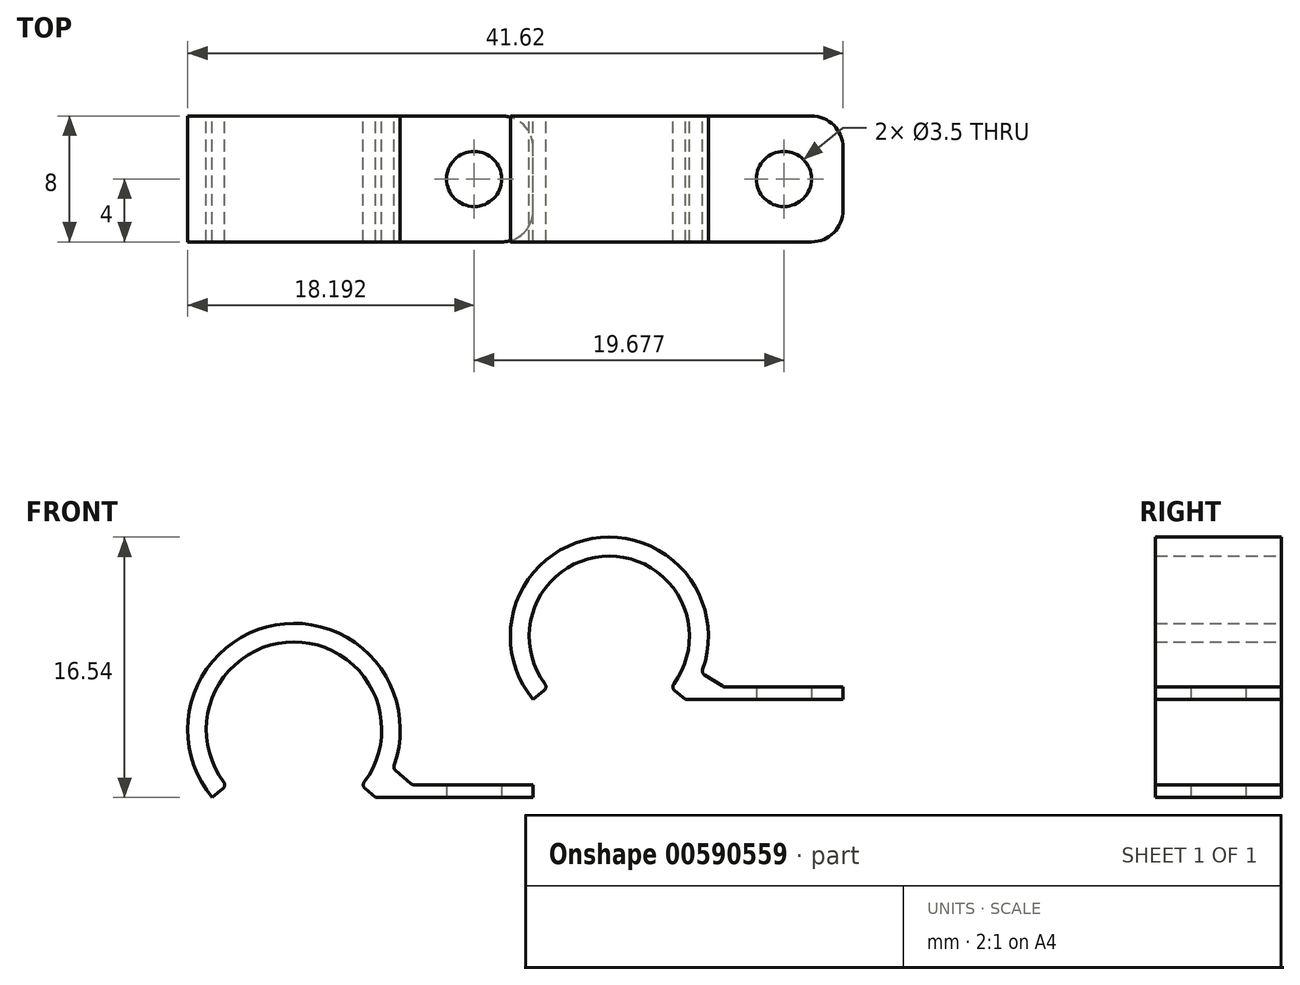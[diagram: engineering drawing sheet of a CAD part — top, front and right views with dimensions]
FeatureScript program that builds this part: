
annotation { "Feature Type Name" : "Feature", "Feature Type Description" : "" }
export const myFeature = defineFeature(function(context is Context, id is Id, definition is map)
    precondition{}
    {
        {
            var Q0;
            Q0=qCreatedBy(makeId("Front.planeOp"),FACE);
            var sketch = newSketch(context, id + "F0", { "sketchPlane" : qUnion([Q0])});
            skArc(sketch, "E0", {"start": v(-11.13, 19.13) * mm, "mid": v(-11.18, 8) * mm, "end": v(-11.03, 19.13) * mm});
            skArc(sketch, "E1", {"start": v(-12.13, 20.56) * mm, "mid": v(-11.18, 6.5) * mm, "end": v(-10.03, 20.55) * mm});
            skLineSegment(sketch, "E2", {"start": v(-12.13, 19.04) * mm, "end": v(-12.13, 31.04) * mm});
            skLineSegment(sketch, "E3", {"start": v(-12.13, 31.04) * mm, "end": v(-11.13, 31.04) * mm});
            skLineSegment(sketch, "E4", {"start": v(-11.13, 31.04) * mm, "end": v(-11.13, 19.13) * mm});
            skLineSegment(sketch, "E5", {"start": v(-10.03, 19.02) * mm, "end": v(-10.03, 31.04) * mm});
            skLineSegment(sketch, "E6", {"start": v(-10.03, 31.04) * mm, "end": v(-11.03, 31.04) * mm});
            skLineSegment(sketch, "E7", {"start": v(-11.03, 31.04) * mm, "end": v(-11.03, 19.13) * mm});
            skArc(sketch, "E8", {"start": v(8.04, 19.7) * mm, "mid": v(8.99, 6.6) * mm, "end": v(10.14, 19.7) * mm});
            skLineSegment(sketch, "E9", {"start": v(8.04, 18.19) * mm, "end": v(8.04, 30.68) * mm});
            skLineSegment(sketch, "E10", {"start": v(8.04, 30.68) * mm, "end": v(9.04, 30.68) * mm});
            skLineSegment(sketch, "E11", {"start": v(9.04, 30.68) * mm, "end": v(9.04, 18.29) * mm});
            skLineSegment(sketch, "E12", {"start": v(10.14, 18.17) * mm, "end": v(10.14, 30.68) * mm});
            skLineSegment(sketch, "E13", {"start": v(10.14, 30.68) * mm, "end": v(9.14, 30.68) * mm});
            skLineSegment(sketch, "E14", {"start": v(9.14, 30.68) * mm, "end": v(9.14, 18.28) * mm});
            skArc(sketch, "E15", {"start": v(9.04, 18.29) * mm, "mid": v(8.99, 8.1) * mm, "end": v(9.14, 18.28) * mm});
            skCircle(sketch, "E16", {"center": v(-11.13, 7.24) * mm, "radius": 0.5 * mm});
            skCircle(sketch, "E17", {"center": v(9.04, 7.36) * mm, "radius": 0.5 * mm});
            skCircle(sketch, "E18", {"center": v(-11.13, 7.24) * mm, "radius": 0.45 * mm});
            skCircle(sketch, "E19", {"center": v(9.04, 7.36) * mm, "radius": 0.45 * mm});
            skLineSegment(sketch, "E20", {"start": v(-11.13, 8) * mm, "end": v(-11.13, 6.5) * mm});
            skLineSegment(sketch, "E21", {"start": v(9.04, 8.1) * mm, "end": v(9.04, 7.86) * mm});
            skLineSegment(sketch, "E22.trimOffspring", {"start": v(9.04, 6.86) * mm, "end": v(9.04, 6.6) * mm});
            skArc(sketch, "E23", {"start": v(8.78, 8.11) * mm, "mid": v(8.2, 7.38) * mm, "end": v(8.75, 6.61) * mm});
            skArc(sketch, "E24", {"start": v(9.36, 6.61) * mm, "mid": v(9.87, 7.36) * mm, "end": v(9.37, 8.12) * mm});
            skArc(sketch, "E25", {"start": v(8.7, 8.12) * mm, "mid": v(8.14, 7.39) * mm, "end": v(8.64, 6.62) * mm});
            skArc(sketch, "E26", {"start": v(9.47, 6.62) * mm, "mid": v(9.93, 7.38) * mm, "end": v(9.46, 8.12) * mm});
            skArc(sketch, "E27.converted", {"start": v(36.32, 10.08) * mm, "mid": v(31.86, 18.98) * mm, "end": v(27.4, 10.08) * mm});
            skArc(sketch, "E28.converted", {"start": v(38.22, 11.15) * mm, "mid": v(30.68, 20.06) * mm, "end": v(26.67, 9.1) * mm});
            skLineSegment(sketch, "E29", {"start": v(37.05, 9.1) * mm, "end": v(47.05, 9.1) * mm});
            skLineSegment(sketch, "E30", {"start": v(47.05, 9.1) * mm, "end": v(47.05, 9.9) * mm});
            skLineSegment(sketch, "E31", {"start": v(47.05, 9.9) * mm, "end": v(39.5, 9.9) * mm});
            skLineSegment(sketch, "E32", {"start": v(27.35, 9.67) * mm, "end": v(26.67, 9.1) * mm});
            skLineSegment(sketch, "E33", {"start": v(36.37, 9.67) * mm, "end": v(37.05, 9.1) * mm});
            skPoint(sketch, "E34.visualSharp", {"position": v(27.58, 9.85) * mm});
            skArc(sketch, "E34.filletArc", {"start": v(27.35, 9.67) * mm, "mid": v(27.46, 9.86) * mm, "end": v(27.4, 10.08) * mm});
            skPoint(sketch, "E35.visualSharp", {"position": v(36.14, 9.85) * mm});
            skArc(sketch, "E35.filletArc", {"start": v(36.32, 10.08) * mm, "mid": v(36.26, 9.86) * mm, "end": v(36.37, 9.67) * mm});
            skLineSegment(sketch, "E36", {"start": v(38.3, 10.82) * mm, "end": v(39.3, 9.97) * mm});
            skPoint(sketch, "E37.visualSharp", {"position": v(38.15, 10.96) * mm});
            skArc(sketch, "E37.filletArc", {"start": v(38.22, 11.15) * mm, "mid": v(38.21, 10.97) * mm, "end": v(38.3, 10.82) * mm});
            skPoint(sketch, "E38.visualSharp", {"position": v(39.4, 9.9) * mm});
            skArc(sketch, "E38.filletArc", {"start": v(39.3, 9.97) * mm, "mid": v(39.4, 9.92) * mm, "end": v(39.5, 9.9) * mm});
            skArc(sketch, "E39.converted", {"start": v(55.98, 16.32) * mm, "mid": v(51.9, 24.44) * mm, "end": v(47.8, 16.32) * mm});
            skArc(sketch, "E40.converted", {"start": v(57.82, 17.24) * mm, "mid": v(50.8, 25.54) * mm, "end": v(47.05, 15.33) * mm});
            skLineSegment(sketch, "E41", {"start": v(56.73, 15.33) * mm, "end": v(66.73, 15.33) * mm});
            skLineSegment(sketch, "E42", {"start": v(66.73, 15.33) * mm, "end": v(66.73, 16.13) * mm});
            skLineSegment(sketch, "E43", {"start": v(66.73, 16.13) * mm, "end": v(59.23, 16.13) * mm});
            skLineSegment(sketch, "E44", {"start": v(47.75, 15.9) * mm, "end": v(47.05, 15.33) * mm});
            skLineSegment(sketch, "E45", {"start": v(56.03, 15.9) * mm, "end": v(56.73, 15.33) * mm});
            skArc(sketch, "E46.filletArc", {"start": v(47.75, 15.9) * mm, "mid": v(47.86, 16.1) * mm, "end": v(47.8, 16.32) * mm});
            skArc(sketch, "E47.filletArc", {"start": v(55.98, 16.32) * mm, "mid": v(55.92, 16.1) * mm, "end": v(56.03, 15.9) * mm});
            skLineSegment(sketch, "E48", {"start": v(57.94, 16.88) * mm, "end": v(59.07, 16.17) * mm});
            skArc(sketch, "E49.filletArc", {"start": v(57.82, 17.24) * mm, "mid": v(57.82, 17.04) * mm, "end": v(57.94, 16.88) * mm});
            skArc(sketch, "E50.filletArc", {"start": v(59.07, 16.17) * mm, "mid": v(59.15, 16.14) * mm, "end": v(59.23, 16.13) * mm});
            skSolve(sketch);
        }
        {
            var Q0;
            Q0=makeQuery(id+"F0.imprint","IMPRINT",FACE,{"disambiguationData":[TD([[makeQuery(id+"F0.imprint","IMPRINT",EDGE,{"derivedFrom":sQuery(id+"F0.wireOp",EDGE,"E27.converted")}),-1.0]])]});
            var Q1;
            Q1=makeQuery(id+"F0.imprint","IMPRINT",FACE,{"disambiguationData":[TD([[makeQuery(id+"F0.imprint","IMPRINT",EDGE,{"derivedFrom":sQuery(id+"F0.wireOp",EDGE,"E39.converted")}),-1.0]])]});
            extrude(context, id + "F1", {"entities" : qUnion([Q0, Q1]), "depth" : 8 * mm, "offsetDistance" : 25 * mm});
        }
        {
            var Q0;
            Q0=makeQuery(id+"F1.opExtrude","SWEPT_FACE",FACE,{"disambiguationData":[OSD([sQuery(id+"F0.wireOp",EDGE,"E29")])]});
            var sketch = newSketch(context, id + "F2", { "sketchPlane" : qUnion([Q0])});
            skCircle(sketch, "E51", {"center": v(43.3, 4) * mm, "radius": 1.75 * mm});
            skLineSegment(sketch, "E52", {"start": v(47.05, 4) * mm, "end": v(38.13, 4) * mm});
            skSolve(sketch);
        }
        {
            var Q0;
            Q0=makeQuery(id+"F1.opExtrude","SWEPT_FACE",FACE,{"disambiguationData":[OSD([sQuery(id+"F0.wireOp",EDGE,"E41")])]});
            var sketch = newSketch(context, id + "F3", { "sketchPlane" : qUnion([Q0])});
            skLineSegment(sketch, "E53", {"start": v(66.73, 4) * mm, "end": v(58.03, 4) * mm});
            skPoint(sketch, "E53.endSnap0", {"position": v(66.73, 4) * mm});
            skCircle(sketch, "E54", {"center": v(62.98, 4) * mm, "radius": 1.75 * mm});
            skSolve(sketch);
        }
        {
            var Q0;
            {var subQ0=sQuery(id+"F2.wireOp",EDGE,"E52");var subQ1=sQuery(id+"F2.wireOp",EDGE,"E51");var subQ2=makeQuery(id+"F2.imprint","INTERSECT",VERTEX,{"disambiguationData":[OD(0.0)],"derivedFrom":[subQ1,subQ0]});Q0=makeQuery(id+"F2.imprint","IMPRINT",FACE,{"disambiguationData":[TD([[makeQuery(id+"F2.imprint","IMPRINT",EDGE,{"disambiguationData":[TD([[subQ2,1.0]])],"derivedFrom":subQ1}),1.0]])]});}
            var Q1;
            {var subQ0=sQuery(id+"F2.wireOp",EDGE,"E52");var subQ1=sQuery(id+"F2.wireOp",EDGE,"E51");var subQ2=makeQuery(id+"F2.imprint","INTERSECT",VERTEX,{"disambiguationData":[OD(0.0)],"derivedFrom":[subQ1,subQ0]});Q1=makeQuery(id+"F2.imprint","IMPRINT",FACE,{"disambiguationData":[TD([[makeQuery(id+"F2.imprint","IMPRINT",EDGE,{"disambiguationData":[TD([[subQ2,-1.0]])],"derivedFrom":subQ1}),1.0]])]});}
            var Q2;
            {var subQ0=sQuery(id+"F3.wireOp",EDGE,"E54");var subQ1=sQuery(id+"F3.wireOp",EDGE,"E53");var subQ2=makeQuery(id+"F3.imprint","INTERSECT",VERTEX,{"disambiguationData":[OD(0.0)],"derivedFrom":[subQ1,subQ0]});Q2=makeQuery(id+"F3.imprint","IMPRINT",FACE,{"disambiguationData":[TD([[makeQuery(id+"F3.imprint","IMPRINT",EDGE,{"disambiguationData":[TD([[subQ2,1.0]])],"derivedFrom":subQ1}),1.0]])]});}
            var Q3;
            {var subQ0=sQuery(id+"F3.wireOp",EDGE,"E54");var subQ1=sQuery(id+"F3.wireOp",EDGE,"E53");var subQ2=makeQuery(id+"F3.imprint","INTERSECT",VERTEX,{"disambiguationData":[OD(0.0)],"derivedFrom":[subQ1,subQ0]});Q3=makeQuery(id+"F3.imprint","IMPRINT",FACE,{"disambiguationData":[TD([[makeQuery(id+"F3.imprint","IMPRINT",EDGE,{"disambiguationData":[TD([[subQ2,1.0]])],"derivedFrom":subQ1}),-1.0]])]});}
            extrude(context, id + "F4", {"entities" : qUnion([Q0, Q1, Q2, Q3]), "operationType" : NewBodyOperationType.REMOVE, "oppositeDirection" : true, "depth" : 25 * mm, "offsetDistance" : 25 * mm});
        }
        {
            var Q0;
            Q0=makeQuery(id+"F1.opExtrude","CAP_EDGE",EDGE,{"disambiguationData":[OSD([sQuery(id+"F0.wireOp",EDGE,"E30")])],"isStart":false});
            var Q1;
            Q1=makeQuery(id+"F1.opExtrude","CAP_EDGE",EDGE,{"disambiguationData":[OSD([sQuery(id+"F0.wireOp",EDGE,"E30")])],"isStart":true});
            var Q2;
            Q2=makeQuery(id+"F1.opExtrude","CAP_EDGE",EDGE,{"disambiguationData":[OSD([sQuery(id+"F0.wireOp",EDGE,"E42")])],"isStart":false});
            var Q3;
            Q3=makeQuery(id+"F1.opExtrude","CAP_EDGE",EDGE,{"disambiguationData":[OSD([sQuery(id+"F0.wireOp",EDGE,"E42")])],"isStart":true});
            fillet(context, id + "F5", {"entities" : qUnion([Q0, Q1, Q2, Q3]), "radius" : 2 * mm, "tangentPropagation" : true, "allowEdgeOverflow" : false});
        }
    });
